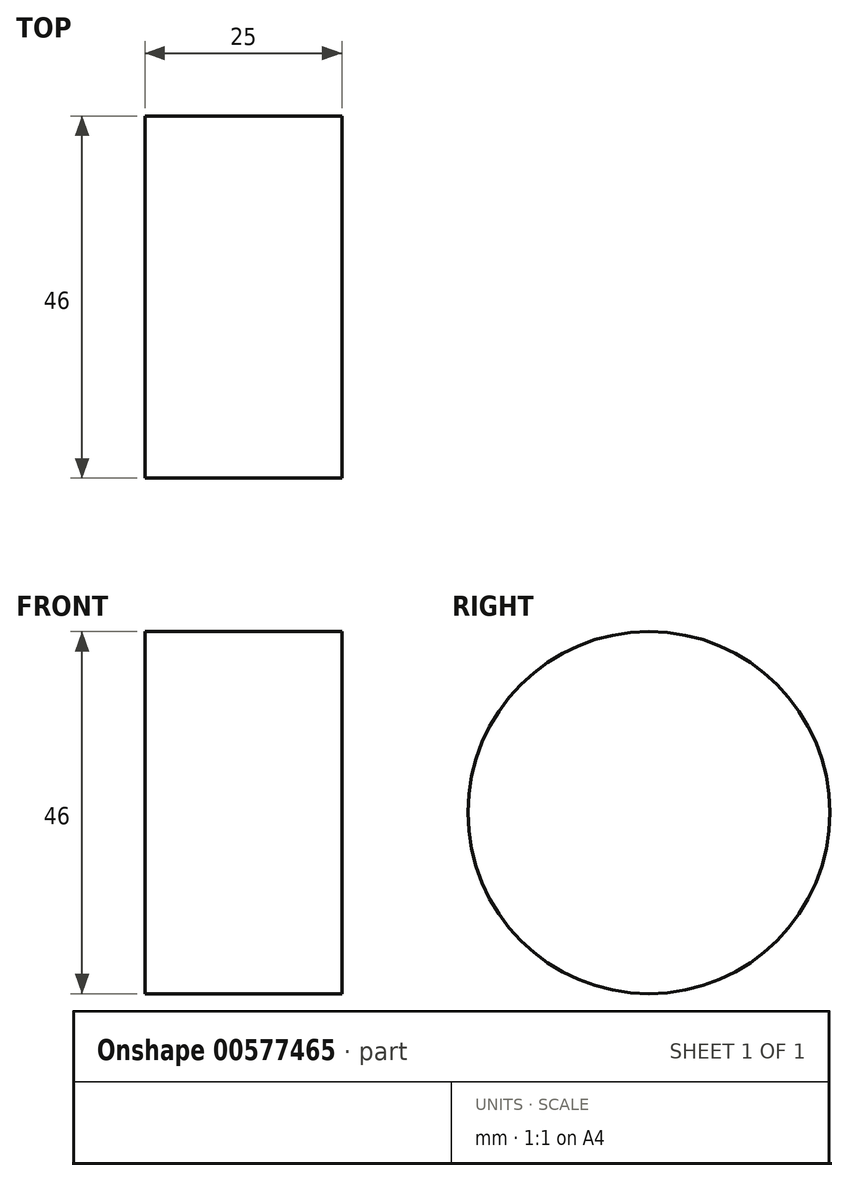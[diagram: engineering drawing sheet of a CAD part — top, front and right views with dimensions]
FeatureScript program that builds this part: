
annotation { "Feature Type Name" : "Feature", "Feature Type Description" : "" }
export const myFeature = defineFeature(function(context is Context, id is Id, definition is map)
    precondition{}
    {
        {
            var Q0;
            Q0=qCreatedBy(makeId("Right.planeOp"),FACE);
            var sketch = newSketch(context, id + "F0", { "sketchPlane" : qUnion([Q0])});
            skCircle(sketch, "E0", {"center": v(0, 0) * mm, "radius": 23 * mm});
            skSolve(sketch);
        }
        {
            var Q0;
            Q0 = qSketchRegion(id + "F0", true);
            extrude(context, id + "F1", {"entities" : qUnion([Q0]), "depth" : 25 * mm, "offsetDistance" : 25 * mm});
        }
    });
